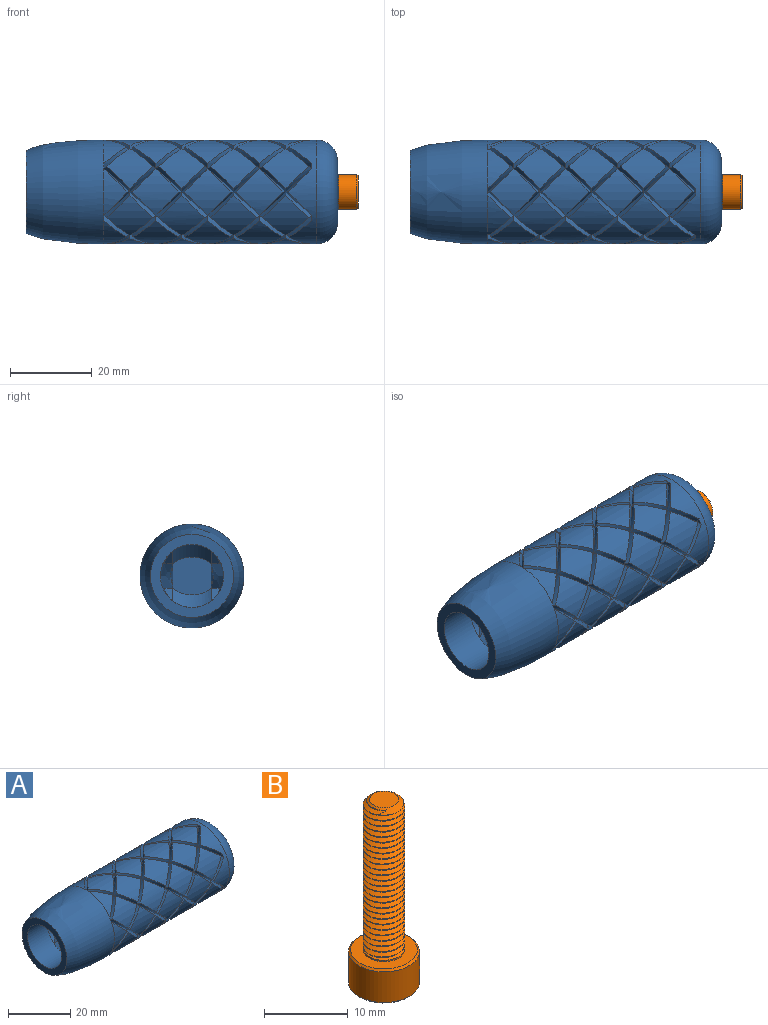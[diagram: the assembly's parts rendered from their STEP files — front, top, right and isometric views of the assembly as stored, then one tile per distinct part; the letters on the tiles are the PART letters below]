
ASSEMBLY  parts=2 mates=1
PART A: 280 faces, bbox 76.2x27.9x28 mm
  f0: bspline ~12.16x11.01mm, area 11.6mm2, adj f8,f18,f26,f229,f276
  f1: bspline ~17.6x16.24mm, area 11.6mm2, adj f9,f20,f22,f227
  f2: bspline ~12.16x11.01mm, area 11.6mm2, adj f10,f16,f24,f228
  f3: bspline ~12.16x9.32mm, area 11.6mm2, adj f11,f23,f225,f247
  f4: bspline ~12.16x9.32mm, area 11.6mm2, adj f12,f25,f30,f226
  f5: bspline ~12.16x10.1mm, area 11.6mm2, adj f13,f21,f29,f238
  f6: bspline ~12.16x11.3mm, area 11.6mm2, adj f14,f27,f31,f239
  f7: bspline ~12.16x11.7mm, area 11.6mm2, adj f15,f17,f28,f237
  f8: bspline ~12.16x11.01mm, area 11.6mm2, adj f0,f149,f242,f276
  f9: bspline ~12.16x11.79mm, area 11.6mm2, adj f1,f142,f145,f220
  f10: bspline ~12.16x11.01mm, area 11.6mm2, adj f2,f144,f147,f219
  f11: bspline ~12.16x9.32mm, area 11.6mm2, adj f3,f146,f154,f215
  f12: bspline ~12.16x9.32mm, area 11.6mm2, adj f4,f148,f166,f208
  f13: bspline ~17.6x12.62mm, area 11.6mm2, adj f5,f143,f165,f209
  f14: bspline ~12.16x11.3mm, area 11.6mm2, adj f6,f162,f167,f207
  f15: bspline ~12.16x11.7mm, area 11.6mm2, adj f7,f163,f164,f210
  f16: bspline ~12.16x11.01mm, area 11.6mm2, adj f2,f22,f118,f228
  f17: bspline ~17.6x16.57mm, area 11.6mm2, adj f7,f29,f55,f237
  f18: bspline ~12.16x11.01mm, area 11.6mm2, adj f0,f19,f117,f229,f276
  f19: bspline ~12.16x11.01mm, area 11.6mm2, adj f18,f119,f242,f276
  f20: bspline ~17.6x12.62mm, area 11.6mm2, adj f1,f21,f120,f227
  f21: bspline ~12.16x10.1mm, area 11.6mm2, adj f5,f20,f54,f238
  f22: bspline ~12.16x11.01mm, area 11.6mm2, adj f1,f16,f120,f227
  f23: bspline ~12.16x11.53mm, area 11.6mm2, adj f3,f24,f225,f245
  f24: bspline ~12.16x11.53mm, area 11.6mm2, adj f2,f23,f118,f228
  f25: bspline ~12.16x11.53mm, area 11.6mm2, adj f4,f26,f121,f226
  f26: bspline ~12.16x11.53mm, area 11.6mm2, adj f0,f25,f117,f229
  f27: bspline ~12.16x11.7mm, area 11.6mm2, adj f6,f28,f53,f239
  f28: bspline ~12.16x11.7mm, area 11.6mm2, adj f7,f27,f55,f237
  f29: bspline ~12.16x10.66mm, area 11.6mm2, adj f5,f17,f54,f238
  f30: bspline ~12.16x9.32mm, area 11.6mm2, adj f4,f31,f121,f226
  f31: bspline ~12.16x9.32mm, area 11.6mm2, adj f6,f30,f53,f239
  f32: bspline ~12.16x9.32mm, area 11.6mm2, adj f34,f107,f177,f201
  f33: bspline ~12.16x11.01mm, area 11.6mm2, adj f35,f175,f176,f202,f272
  f34: bspline ~12.16x9.32mm, area 11.6mm2, adj f32,f83,f191,f192
  f35: bspline ~12.16x11.01mm, area 11.6mm2, adj f33,f190,f242,f272
  f36: bspline ~17.6x16.24mm, area 11.6mm2, adj f39,f168,f173,f203
  f37: bspline ~12.16x9.32mm, area 11.6mm2, adj f40,f171,f205,f243
  f38: bspline ~12.16x11.01mm, area 11.6mm2, adj f41,f169,f170,f206
  f39: bspline ~12.16x11.79mm, area 11.6mm2, adj f36,f184,f188,f194
  f40: bspline ~12.16x9.32mm, area 11.6mm2, adj f37,f80,f187,f195
  f41: bspline ~12.16x11.01mm, area 11.6mm2, adj f38,f185,f186,f196
  f42: bspline ~12.16x11.7mm, area 11.6mm2, adj f43,f105,f242,f271
  f43: bspline ~12.16x11.7mm, area 11.6mm2, adj f42,f83,f191,f192,f271
  f44: bspline ~17.6x16.24mm, area 11.6mm2, adj f47,f178,f183,f197
  f45: bspline ~12.16x11.7mm, area 11.6mm2, adj f48,f97,f181,f199
  f46: bspline ~12.16x10.1mm, area 11.6mm2, adj f49,f179,f180,f200
  f47: bspline ~12.16x11.79mm, area 11.6mm2, adj f44,f184,f188,f194
  f48: bspline ~12.16x11.7mm, area 11.6mm2, adj f45,f80,f187,f195
  f49: bspline ~17.6x12.62mm, area 11.6mm2, adj f46,f185,f186,f196
  f50: bspline ~12.16x9.74mm, area 11.6mm2, adj f53,f178,f183,f197
  f51: bspline ~17.6x16.57mm, area 11.6mm2, adj f54,f97,f181,f199
  f52: bspline ~12.16x10.66mm, area 11.6mm2, adj f55,f179,f180,f200
  f53: bspline ~12.16x9.74mm, area 11.6mm2, adj f27,f31,f50,f239
  f54: bspline ~12.16x10.66mm, area 11.6mm2, adj f21,f29,f51,f238
  f55: bspline ~17.6x16.57mm, area 11.6mm2, adj f17,f28,f52,f237
  f56: bspline ~12.16x9.74mm, area 11.6mm2, adj f59,f156,f161,f211,f273
  f57: bspline ~12.16x11.53mm, area 11.6mm2, adj f60,f137,f159,f212
  f58: bspline ~12.16x11.53mm, area 11.6mm2, adj f61,f157,f158,f213
  f59: bspline ~12.16x9.74mm, area 11.6mm2, adj f56,f174,f242,f273
  f60: bspline ~12.16x11.53mm, area 11.6mm2, adj f57,f107,f177,f201
  f61: bspline ~12.16x11.53mm, area 11.6mm2, adj f58,f175,f176,f202
  f62: bspline ~12.16x9.74mm, area 11.6mm2, adj f64,f150,f153,f216
  f63: bspline ~12.16x11.53mm, area 11.6mm2, adj f65,f151,f218,f248
  f64: bspline ~12.16x9.74mm, area 11.6mm2, adj f62,f168,f173,f203
  f65: bspline ~12.16x11.53mm, area 11.6mm2, adj f63,f169,f170,f206
  f66: bspline ~12.16x11.3mm, area 11.6mm2, adj f69,f162,f167,f207
  f67: bspline ~12.16x11.01mm, area 11.6mm2, adj f70,f143,f165,f209
  f68: bspline ~12.16x9.32mm, area 11.6mm2, adj f71,f163,f164,f210
  f69: bspline ~12.16x11.3mm, area 11.6mm2, adj f66,f156,f161,f211
  f70: bspline ~12.16x11.01mm, area 11.6mm2, adj f67,f137,f159,f212
  f71: bspline ~12.16x9.32mm, area 11.6mm2, adj f68,f157,f158,f213
  f72: bspline ~12.16x11.3mm, area 11.6mm2, adj f73,f155,f214,f246
  f73: bspline ~12.16x11.3mm, area 11.6mm2, adj f72,f150,f153,f216
  f74: bspline ~12.16x11.7mm, area 11.6mm2, adj f76,f108,f111,f224
  f75: bspline ~12.16x11.3mm, area 11.6mm2, adj f77,f106,f109,f223
  f76: bspline ~12.16x11.7mm, area 11.6mm2, adj f74,f84,f87,f236
  f77: bspline ~12.16x11.3mm, area 11.6mm2, adj f75,f82,f85,f235
  f78: bspline ~12.16x10.1mm, area 11.6mm2, adj f79,f110,f172,f204
  f79: bspline ~17.6x12.62mm, area 11.6mm2, adj f78,f86,f189,f193
  f80: bspline ~12.16x11.3mm, area 11.6mm2, adj f40,f48,f81,f195
  f81: bspline ~12.16x11.3mm, area 11.6mm2, adj f80,f95,f234,f243
  f82: bspline ~12.16x11.3mm, area 11.6mm2, adj f77,f83,f93,f235
  f83: bspline ~12.16x11.3mm, area 11.6mm2, adj f34,f43,f82,f192
  f84: bspline ~12.16x11.3mm, area 11.6mm2, adj f76,f85,f92,f236
  f85: bspline ~12.16x11.3mm, area 11.6mm2, adj f77,f84,f93,f235
  f86: bspline ~12.16x9.74mm, area 11.6mm2, adj f79,f87,f89,f193
  f87: bspline ~12.16x9.74mm, area 11.6mm2, adj f76,f86,f92,f236
  f88: bspline ~12.16x11.01mm, area 11.6mm2, adj f89,f102,f182,f198
  f89: bspline ~12.16x11.01mm, area 11.6mm2, adj f86,f88,f189,f193
  f90: bspline ~12.16x9.32mm, area 11.6mm2, adj f92,f100,f103,f233
  f91: bspline ~12.16x11.3mm, area 11.6mm2, adj f93,f101,f104,f231
  f92: bspline ~12.16x9.32mm, area 11.6mm2, adj f84,f87,f90,f236
  f93: bspline ~12.16x11.3mm, area 11.6mm2, adj f82,f85,f91,f235
  f94: bspline ~12.16x11.3mm, area 11.6mm2, adj f95,f96,f99,f230
  f95: bspline ~12.16x11.3mm, area 11.6mm2, adj f81,f94,f234,f244
  f96: bspline ~12.16x11.7mm, area 11.6mm2, adj f94,f97,f115,f230
  f97: bspline ~12.16x11.7mm, area 11.6mm2, adj f45,f51,f96,f199
  f98: bspline ~12.16x9.32mm, area 11.6mm2, adj f99,f113,f232,f244
  f99: bspline ~12.16x9.32mm, area 11.6mm2, adj f94,f98,f115,f230
  f100: bspline ~12.16x9.32mm, area 11.6mm2, adj f90,f101,f112,f233
  f101: bspline ~12.16x9.32mm, area 11.6mm2, adj f91,f100,f114,f231
  f102: bspline ~12.16x11.53mm, area 11.6mm2, adj f88,f103,f116,f198
  f103: bspline ~12.16x11.53mm, area 11.6mm2, adj f90,f102,f112,f233
  f104: bspline ~12.16x11.7mm, area 11.6mm2, adj f91,f105,f114,f231,f275
  f105: bspline ~12.16x11.7mm, area 11.6mm2, adj f42,f104,f242,f275
  f106: bspline ~12.16x9.32mm, area 11.6mm2, adj f75,f107,f125,f223
  f107: bspline ~12.16x9.32mm, area 11.6mm2, adj f32,f60,f106,f201
  f108: bspline ~12.16x11.7mm, area 11.6mm2, adj f74,f109,f124,f224
  f109: bspline ~12.16x11.7mm, area 11.6mm2, adj f75,f108,f125,f223
  f110: bspline ~12.16x10.66mm, area 11.6mm2, adj f78,f111,f127,f204
  f111: bspline ~17.6x16.57mm, area 11.6mm2, adj f74,f110,f124,f224
  f112: bspline ~12.16x11.53mm, area 11.6mm2, adj f100,f103,f117,f233
  f113: bspline ~12.16x11.53mm, area 11.6mm2, adj f98,f118,f232,f245
  f114: bspline ~12.16x9.74mm, area 11.6mm2, adj f101,f104,f119,f231,f275
  f115: bspline ~12.16x9.74mm, area 11.6mm2, adj f96,f99,f120,f230
  f116: bspline ~12.16x11.53mm, area 11.6mm2, adj f102,f121,f182,f198
  f117: bspline ~12.16x11.53mm, area 11.6mm2, adj f18,f26,f112,f229
  f118: bspline ~12.16x11.53mm, area 11.6mm2, adj f16,f24,f113,f228
  f119: bspline ~12.16x9.74mm, area 11.6mm2, adj f19,f114,f242,f275
  f120: bspline ~12.16x9.74mm, area 11.6mm2, adj f20,f22,f115,f227
  f121: bspline ~12.16x11.53mm, area 11.6mm2, adj f25,f30,f116,f226
  f122: bspline ~12.16x10.66mm, area 11.6mm2, adj f124,f138,f141,f221
  f123: bspline ~12.16x9.74mm, area 11.6mm2, adj f125,f136,f139,f222
  f124: bspline ~17.6x16.57mm, area 11.6mm2, adj f108,f111,f122,f224
  f125: bspline ~12.16x9.74mm, area 11.6mm2, adj f106,f109,f123,f223
  f126: bspline ~17.6x16.57mm, area 11.6mm2, adj f127,f140,f152,f217
  f127: bspline ~12.16x10.66mm, area 11.6mm2, adj f110,f126,f172,f204
  f128: bspline ~17.6x12.62mm, area 11.6mm2, adj f131,f144,f147,f219
  f129: bspline ~12.16x11.79mm, area 11.6mm2, adj f132,f142,f145,f220
  f130: bspline ~12.16x11.7mm, area 11.6mm2, adj f133,f148,f166,f208,f274
  f131: bspline ~12.16x10.1mm, area 11.6mm2, adj f128,f138,f141,f221
  f132: bspline ~17.6x16.24mm, area 11.6mm2, adj f129,f136,f139,f222
  f133: bspline ~12.16x11.7mm, area 11.6mm2, adj f130,f160,f242,f274
  f134: bspline ~12.16x11.7mm, area 11.6mm2, adj f135,f146,f154,f215
  f135: bspline ~12.16x11.7mm, area 11.6mm2, adj f134,f140,f152,f217
  f136: bspline ~12.16x11.01mm, area 11.6mm2, adj f123,f132,f137,f222
  f137: bspline ~12.16x11.01mm, area 11.6mm2, adj f57,f70,f136,f212
  f138: bspline ~12.16x10.1mm, area 11.6mm2, adj f122,f131,f139,f221
  f139: bspline ~17.6x12.62mm, area 11.6mm2, adj f123,f132,f138,f222
  f140: bspline ~17.6x16.57mm, area 11.6mm2, adj f126,f135,f141,f217
  f141: bspline ~12.16x10.66mm, area 11.6mm2, adj f122,f131,f140,f221
  f142: bspline ~12.16x11.79mm, area 11.6mm2, adj f9,f129,f143,f220
  f143: bspline ~17.6x16.24mm, area 11.6mm2, adj f13,f67,f142,f209
  f144: bspline ~17.6x16.24mm, area 11.6mm2, adj f10,f128,f145,f219
  f145: bspline ~12.16x11.79mm, area 11.6mm2, adj f9,f129,f144,f220
  f146: bspline ~12.16x9.74mm, area 11.6mm2, adj f11,f134,f147,f215
  f147: bspline ~12.16x9.74mm, area 11.6mm2, adj f10,f128,f146,f219
  f148: bspline ~12.16x9.74mm, area 11.6mm2, adj f12,f130,f149,f208,f274
  f149: bspline ~12.16x9.74mm, area 11.6mm2, adj f8,f148,f242,f274
  f150: bspline ~12.16x9.32mm, area 11.6mm2, adj f62,f73,f151,f216
  f151: bspline ~12.16x9.32mm, area 11.6mm2, adj f63,f150,f218,f246
  f152: bspline ~12.16x11.7mm, area 11.6mm2, adj f126,f135,f153,f217
  f153: bspline ~12.16x11.7mm, area 11.6mm2, adj f62,f73,f152,f216
  f154: bspline ~12.16x11.3mm, area 11.6mm2, adj f11,f134,f155,f215
  f155: bspline ~12.16x11.3mm, area 11.6mm2, adj f72,f154,f214,f247
  f156: bspline ~12.16x9.32mm, area 11.6mm2, adj f56,f69,f157,f211
  f157: bspline ~12.16x9.32mm, area 11.6mm2, adj f58,f71,f156,f213
  f158: bspline ~12.16x11.53mm, area 11.6mm2, adj f58,f71,f159,f213
  f159: bspline ~12.16x11.53mm, area 11.6mm2, adj f57,f70,f158,f212
  f160: bspline ~12.16x11.7mm, area 11.6mm2, adj f133,f161,f242,f273
  f161: bspline ~12.16x11.7mm, area 11.6mm2, adj f56,f69,f160,f211,f273
  f162: bspline ~12.16x11.3mm, area 11.6mm2, adj f14,f66,f163,f207
  f163: bspline ~12.16x11.3mm, area 11.6mm2, adj f15,f68,f162,f210
  f164: bspline ~12.16x9.74mm, area 11.6mm2, adj f15,f68,f165,f210
  f165: bspline ~12.16x9.74mm, area 11.6mm2, adj f13,f67,f164,f209
  f166: bspline ~12.16x11.3mm, area 11.6mm2, adj f12,f130,f167,f208
  f167: bspline ~12.16x11.3mm, area 11.6mm2, adj f14,f66,f166,f207
  f168: bspline ~12.16x11.01mm, area 11.6mm2, adj f36,f64,f169,f203
  f169: bspline ~12.16x11.01mm, area 11.6mm2, adj f38,f65,f168,f206
  f170: bspline ~12.16x11.53mm, area 11.6mm2, adj f38,f65,f171,f206
  f171: bspline ~12.16x11.53mm, area 11.6mm2, adj f37,f170,f205,f248
  f172: bspline ~12.16x10.1mm, area 11.6mm2, adj f78,f127,f173,f204
  f173: bspline ~17.6x12.62mm, area 11.6mm2, adj f36,f64,f172,f203
  f174: bspline ~12.16x11.01mm, area 11.6mm2, adj f59,f175,f242,f272
  f175: bspline ~12.16x11.01mm, area 11.6mm2, adj f33,f61,f174,f202,f272
  f176: bspline ~12.16x11.53mm, area 11.6mm2, adj f33,f61,f177,f202
  f177: bspline ~12.16x11.53mm, area 11.6mm2, adj f32,f60,f176,f201
  f178: bspline ~17.6x12.62mm, area 11.6mm2, adj f44,f50,f179,f197
  f179: bspline ~12.16x10.1mm, area 11.6mm2, adj f46,f52,f178,f200
  f180: bspline ~12.16x10.66mm, area 11.6mm2, adj f46,f52,f181,f200
  f181: bspline ~17.6x16.57mm, area 11.6mm2, adj f45,f51,f180,f199
  f182: bspline ~12.16x11.01mm, area 11.6mm2, adj f88,f116,f183,f198
  f183: bspline ~12.16x11.01mm, area 11.6mm2, adj f44,f50,f182,f197
  f184: bspline ~12.16x11.79mm, area 11.6mm2, adj f39,f47,f185,f194
  f185: bspline ~17.6x16.24mm, area 11.6mm2, adj f41,f49,f184,f196
  f186: bspline ~12.16x9.74mm, area 11.6mm2, adj f41,f49,f187,f196
  f187: bspline ~12.16x9.74mm, area 11.6mm2, adj f40,f48,f186,f195
  f188: bspline ~12.16x11.79mm, area 11.6mm2, adj f39,f47,f189,f194
  f189: bspline ~17.6x16.24mm, area 11.6mm2, adj f79,f89,f188,f193
  f190: bspline ~12.16x9.74mm, area 11.6mm2, adj f35,f191,f242,f271
  f191: bspline ~12.16x9.74mm, area 11.6mm2, adj f34,f43,f190,f192,f271
  f192: cylinder r=12.7mm len=11.24mm, axis (-1,0,0), area 66.2mm2, adj f34,f43,f83,f191
  f193: cylinder r=12.7mm len=11.23mm, axis (-1,0,0), area 66mm2, adj f79,f86,f89,f189
  f194: cylinder r=12.7mm len=11.33mm, axis (-1,0,0), area 65.9mm2, adj f39,f47,f184,f188
  f195: cylinder r=12.7mm len=11.24mm, axis (-1,0,0), area 66.2mm2, adj f40,f48,f80,f187
  f196: cylinder r=12.7mm len=11.23mm, axis (-1,0,0), area 66mm2, adj f41,f49,f185,f186
  f197: cylinder r=12.7mm len=11.23mm, axis (-1,0,0), area 66mm2, adj f44,f50,f178,f183
  f198: cylinder r=12.7mm len=11.35mm, axis (-1,0,0), area 66.2mm2, adj f88,f102,f116,f182
  f199: cylinder r=12.7mm len=11.34mm, axis (-1,0,0), area 66mm2, adj f45,f51,f97,f181
  f200: cylinder r=12.7mm len=11.22mm, axis (-1,0,0), area 65.9mm2, adj f46,f52,f179,f180
  f201: cylinder r=12.7mm len=11.25mm, axis (-1,0,0), area 66.2mm2, adj f32,f60,f107,f177
  f202: cylinder r=12.7mm len=11.35mm, axis (-1,0,0), area 66.2mm2, adj f33,f61,f175,f176
  f203: cylinder r=12.7mm len=11.23mm, axis (-1,0,0), area 66mm2, adj f36,f64,f168,f173
  f204: cylinder r=12.7mm len=11.22mm, axis (-1,0,0), area 65.9mm2, adj f78,f110,f127,f172
  f205: cylinder r=12.7mm len=9.84mm, axis (-1,0,0), area 33.1mm2, adj f37,f171,f270
  f206: cylinder r=12.7mm len=11.35mm, axis (-1,0,0), area 66.2mm2, adj f38,f65,f169,f170
  f207: cylinder r=12.7mm len=11.36mm, axis (-1,0,0), area 66.2mm2, adj f14,f66,f162,f167
  f208: cylinder r=12.7mm len=11.24mm, axis (-1,0,0), area 66.2mm2, adj f12,f130,f148,f166
  f209: cylinder r=12.7mm len=11.23mm, axis (-1,0,0), area 66mm2, adj f13,f67,f143,f165
  f210: cylinder r=12.7mm len=11.24mm, axis (-1,0,0), area 66.2mm2, adj f15,f68,f163,f164
  f211: cylinder r=12.7mm len=11.24mm, axis (-1,0,0), area 66.2mm2, adj f56,f69,f156,f161
  f212: cylinder r=12.7mm len=11.35mm, axis (-1,0,0), area 66.2mm2, adj f57,f70,f137,f159
  f213: cylinder r=12.7mm len=11.25mm, axis (-1,0,0), area 66.2mm2, adj f58,f71,f157,f158
  f214: cylinder r=12.7mm len=11.36mm, axis (-1,0,0), area 33.1mm2, adj f72,f155,f270
  f215: cylinder r=12.7mm len=11.24mm, axis (-1,0,0), area 66.2mm2, adj f11,f134,f146,f154
  f216: cylinder r=12.7mm len=11.24mm, axis (-1,0,0), area 66.2mm2, adj f62,f73,f150,f153
  f217: cylinder r=12.7mm len=11.34mm, axis (-1,0,0), area 66mm2, adj f126,f135,f140,f152
  f218: cylinder r=12.7mm len=9.84mm, axis (-1,0,0), area 33.1mm2, adj f63,f151,f270
  f219: cylinder r=12.7mm len=11.23mm, axis (-1,0,0), area 66mm2, adj f10,f128,f144,f147
  f220: cylinder r=12.7mm len=11.33mm, axis (-1,0,0), area 65.9mm2, adj f9,f129,f142,f145
  f221: cylinder r=12.7mm len=11.22mm, axis (-1,0,0), area 65.9mm2, adj f122,f131,f138,f141
  f222: cylinder r=12.7mm len=11.23mm, axis (-1,0,0), area 66mm2, adj f123,f132,f136,f139
  f223: cylinder r=12.7mm len=11.24mm, axis (-1,0,0), area 66.2mm2, adj f75,f106,f109,f125
  f224: cylinder r=12.7mm len=11.34mm, axis (-1,0,0), area 66mm2, adj f74,f108,f111,f124
  f225: cylinder r=12.7mm len=9.84mm, axis (-1,0,0), area 33.1mm2, adj f3,f23,f270
  f226: cylinder r=12.7mm len=11.25mm, axis (-1,0,0), area 66.2mm2, adj f4,f25,f30,f121
  f227: cylinder r=12.7mm len=11.23mm, axis (-1,0,0), area 66mm2, adj f1,f20,f22,f120
  f228: cylinder r=12.7mm len=11.35mm, axis (-1,0,0), area 66.2mm2, adj f2,f16,f24,f118
  f229: cylinder r=12.7mm len=11.35mm, axis (-1,0,0), area 66.2mm2, adj f0,f18,f26,f117
  f230: cylinder r=12.7mm len=11.24mm, axis (-1,0,0), area 66.2mm2, adj f94,f96,f99,f115
  f231: cylinder r=12.7mm len=11.24mm, axis (-1,0,0), area 66.2mm2, adj f91,f101,f104,f114
  f232: cylinder r=12.7mm len=9.84mm, axis (-1,0,0), area 33.1mm2, adj f98,f113,f270
  f233: cylinder r=12.7mm len=11.25mm, axis (-1,0,0), area 66.2mm2, adj f90,f100,f103,f112
  f234: cylinder r=12.7mm len=11.36mm, axis (-1,0,0), area 33.1mm2, adj f81,f95,f270
  f235: cylinder r=12.7mm len=11.36mm, axis (-1,0,0), area 66.2mm2, adj f77,f82,f85,f93
  f236: cylinder r=12.7mm len=11.24mm, axis (-1,0,0), area 66.2mm2, adj f76,f84,f87,f92
  f237: cylinder r=12.7mm len=11.34mm, axis (-1,0,0), area 66mm2, adj f7,f17,f28,f55
  f238: cylinder r=12.7mm len=11.22mm, axis (-1,0,0), area 65.9mm2, adj f5,f21,f29,f54
  f239: cylinder r=12.7mm len=11.24mm, axis (-1,0,0), area 66.2mm2, adj f6,f27,f31,f53
  f240: plane 15.24x15.24mm, normal (1,0,0), area 160.4mm2, adj f241,f277
  f241: torus R=7.62mm, axis (-1,0,0), area 544.2mm2, adj f240,f242
  f242: cylinder r=12.7mm len=25.4mm, axis (-1,0,0), area 299mm2, adj f8,f19,f35,f42,f59,f105,f119,f133
  f243: plane 1.47x1.33mm, normal (1,0,0), area 0.9mm2, adj f37,f81,f270
  f244: plane 1.47x1.33mm, normal (1,0,0), area 0.9mm2, adj f95,f98,f270
  f245: plane 1.53x1.28mm, normal (1,0,0), area 0.9mm2, adj f23,f113,f270
  f246: plane 1.47x1.33mm, normal (1,0,0), area 0.9mm2, adj f72,f151,f270
  f247: plane 1.47x1.33mm, normal (1,0,0), area 0.9mm2, adj f3,f155,f270
  f248: plane 1.53x1.28mm, normal (1,0,0), area 0.9mm2, adj f63,f171,f270
  f249: plane 9.53x9.27mm, normal (-1,0,0), area 78.4mm2, adj f250,f254,f255,f256,f262,f263
  f250: cylinder r=7.73mm len=38.11mm, axis (1,0,0), area 391.3mm2, adj f249,f253,f254,f258,f263,f264
  f251: plane 29.73x2.14mm, normal (0,0,-1), area 31.8mm2, adj f256,f257,f265
  f252: plane 3.09x3.09mm, normal (-0.71,0,0.71), area 5.6mm2, adj f253,f264,f265
  f253: plane 29.73x2.14mm, normal (0,0,1), area 31.8mm2, adj f250,f252,f265
  f254: plane 8.39x2.99mm, normal (0,1,0), area 8.2mm2, adj f249,f250,f265
  f255: plane 8.39x2.99mm, normal (0,1,0), area 8.2mm2, adj f249,f256,f265
  f256: cylinder r=7.73mm len=38.11mm, axis (1,0,0), area 391.3mm2, adj f249,f251,f255,f261,f262,f266
  f257: plane 3.09x3.09mm, normal (-0.71,0,-0.71), area 5.6mm2, adj f251,f265,f266
  f258: plane 29.73x2.14mm, normal (0,0,1), area 31.8mm2, adj f250,f259,f267
  f259: plane 3.09x3.09mm, normal (-0.71,0,0.71), area 5.6mm2, adj f258,f264,f267
  f260: plane 3.09x3.09mm, normal (-0.71,0,-0.71), area 5.6mm2, adj f261,f266,f267
  f261: plane 29.73x2.14mm, normal (0,0,-1), area 31.8mm2, adj f256,f260,f267
  f262: plane 8.39x2.99mm, normal (0,-1,0), area 8.2mm2, adj f249,f256,f267
  f263: plane 8.39x2.99mm, normal (0,-1,0), area 8.2mm2, adj f249,f250,f267
  f264: bspline ~9.53x5.37mm, area 43.3mm2, adj f250,f252,f259,f268
  f265: bspline ~41.2x12.16mm, area 247.8mm2, adj f251,f252,f253,f254,f255,f257,f268
  f266: bspline ~9.53x5.37mm, area 43.3mm2, adj f256,f257,f260,f268
  f267: bspline ~41.2x12.16mm, area 247.8mm2, adj f258,f259,f260,f261,f262,f263,f268
  f268: cylinder r=7.73mm len=15.45mm, axis (1,0,0), area 449.9mm2, adj f264,f265,f266,f267,f269
  f269: plane 20.32x20.32mm, normal (-1,0,0), area 136.8mm2, adj f268,f270
  f270: revolved ~25.4x25.4mm, area 1459.6mm2, adj f205,f214,f218,f225,f232,f234,f243,f244
  f271: plane 1.48x1.34mm, normal (-1,0,0), area 1mm2, adj f42,f43,f190,f191,f242
  f272: plane 1.55x1.28mm, normal (-1,0,0), area 1mm2, adj f33,f35,f174,f175,f242
  f273: plane 1.48x1.34mm, normal (-1,0,0), area 1mm2, adj f56,f59,f160,f161,f242
  f274: plane 1.48x1.34mm, normal (-1,0,0), area 1mm2, adj f130,f133,f148,f149,f242
  f275: plane 1.48x1.34mm, normal (-1,0,0), area 1mm2, adj f104,f105,f114,f119,f242
  f276: plane 1.55x1.28mm, normal (-1,0,0), area 1mm2, adj f0,f8,f18,f19,f242
  f277: cylinder r=2.65mm len=20.23mm, axis (1,0,0), area 336.8mm2, adj f240,f279
  f278: plane 1.3x1.3mm, normal (1,0,0), area 1.3mm2, adj f279
  f279: cone r=0.65mm half-angle=45deg, axis (1,0,0), area 29.3mm2, adj f277,f278
PART B: 51 faces, bbox 9.4x9.4x28 mm
  f0: cone r=2.5mm half-angle=67.5deg, axis (0,0,-1), area 4.1mm2, adj f1,f30,f31,f50
  f1: cylinder r=1.98mm len=21.41mm, axis (0,0,-1), area 33.3mm2, adj f0,f2,f30,f50
  f2: cone r=1.73mm half-angle=55deg, axis (0,0,-1), area 7.9mm2, adj f1,f3,f4,f30,f50
  f3: plane 3.45x3.45mm, normal (0,0,1), area 9.4mm2, adj f2
  f4: cylinder r=2.5mm len=5mm, axis (0,0,1), area 1mm2, adj f2,f5,f30,f50
  f5: cylinder r=2.5mm len=5mm, axis (0,0,1), area 1.6mm2, adj f4,f6,f30,f50
  f6: cylinder r=2.5mm len=5mm, axis (0,0,1), area 1.6mm2, adj f5,f7,f30,f50
  f7: cylinder r=2.5mm len=5mm, axis (0,0,1), area 1.6mm2, adj f6,f8,f30,f50
  f8: cylinder r=2.5mm len=5mm, axis (0,0,1), area 1.6mm2, adj f7,f9,f30,f50
  f9: cylinder r=2.5mm len=5mm, axis (0,0,1), area 1.6mm2, adj f8,f10,f30,f50
  f10: cylinder r=2.5mm len=5mm, axis (0,0,1), area 1.6mm2, adj f9,f11,f30,f50
  f11: cylinder r=2.5mm len=5mm, axis (0,0,1), area 1.6mm2, adj f10,f12,f30,f50
  f12: cylinder r=2.5mm len=5mm, axis (0,0,1), area 1.6mm2, adj f11,f13,f30,f50
  f13: cylinder r=2.5mm len=5mm, axis (0,0,1), area 1.6mm2, adj f12,f14,f30,f50
  f14: cylinder r=2.5mm len=5mm, axis (0,0,1), area 1.6mm2, adj f13,f15,f30,f50
  f15: cylinder r=2.5mm len=5mm, axis (0,0,1), area 1.6mm2, adj f14,f16,f30,f50
  f16: cylinder r=2.5mm len=5mm, axis (0,0,1), area 1.6mm2, adj f15,f17,f30,f50
  f17: cylinder r=2.5mm len=5mm, axis (0,0,1), area 1.6mm2, adj f16,f18,f30,f50
  f18: cylinder r=2.5mm len=5mm, axis (0,0,1), area 1.6mm2, adj f17,f19,f30,f50
  f19: cylinder r=2.5mm len=5mm, axis (0,0,1), area 1.6mm2, adj f18,f20,f30,f50
  f20: cylinder r=2.5mm len=5mm, axis (0,0,1), area 1.6mm2, adj f19,f21,f30,f50
  f21: cylinder r=2.5mm len=5mm, axis (0,0,1), area 1.6mm2, adj f20,f22,f30,f50
  f22: cylinder r=2.5mm len=5mm, axis (0,0,1), area 1.6mm2, adj f21,f23,f30,f50
  f23: cylinder r=2.5mm len=5mm, axis (0,0,1), area 1.6mm2, adj f22,f24,f30,f50
  f24: cylinder r=2.5mm len=5mm, axis (0,0,1), area 1.6mm2, adj f23,f25,f30,f50
  f25: cylinder r=2.5mm len=5mm, axis (0,0,1), area 1.6mm2, adj f24,f26,f30,f50
  f26: cylinder r=2.5mm len=5mm, axis (0,0,1), area 1.6mm2, adj f25,f27,f30,f50
  f27: cylinder r=2.5mm len=5mm, axis (0,0,1), area 1.6mm2, adj f26,f28,f30,f50
  f28: cylinder r=2.5mm len=5mm, axis (0,0,1), area 1.6mm2, adj f27,f29,f30,f50
  f29: cylinder r=2.5mm len=5mm, axis (0,0,1), area 1.6mm2, adj f28,f30,f31,f50
  f30: bspline ~21.71x4.99mm, area 225.4mm2, adj f0,f1,f2,f4,f5,f6,f7,f8
  f31: cylinder r=2.5mm len=5mm, axis (0,0,1), area 4.6mm2, adj f0,f29,f30,f32,f50
  f32: plane 7.99x7.99mm, normal (0,0,1), area 30.5mm2, adj f31,f33
  f33: cone r=4.25mm half-angle=45deg, axis (0,0,-1), area 9.3mm2, adj f32,f34
  f34: cylinder r=4.25mm len=8.5mm, axis (0,0,1), area 119.9mm2, adj f33,f35
  f35: cone r=4mm half-angle=45deg, axis (0,0,1), area 9.3mm2, adj f34,f36
  f36: plane 8.74x8.74mm, normal (0,0,-1), area 33.4mm2, adj f35,f37,f45,f46,f47,f48,f49
  f37: cone r=2.31mm half-angle=45deg, axis (0,0,-1), area 0mm2, adj f36,f38
  f38: plane 3.88x2.88mm, normal (-0.5,-0.87,0), area 6.5mm2, adj f37,f39,f43,f44
  f39: plane 4.62x4mm, normal (0,0,-1), area 13.9mm2, adj f38,f40,f41,f42,f43,f44
  f40: plane 3.22x2.53mm, normal (1,0,0), area 6.5mm2, adj f39,f41,f44,f48
  f41: plane 3.88x2.88mm, normal (0.5,0.87,0), area 6.5mm2, adj f39,f40,f42,f47
  f42: plane 3.88x2.88mm, normal (-0.5,0.87,0), area 6.5mm2, adj f39,f41,f43,f46
  f43: plane 3.88x3.18mm, normal (-1,0,0), area 6.5mm2, adj f38,f39,f42,f45
  f44: plane 3.88x2.88mm, normal (0.5,-0.87,0), area 6.5mm2, adj f38,f39,f40,f49
  f45: cone r=2.31mm half-angle=45deg, axis (0,0,-1), area 0mm2, adj f36,f43
  f46: cone r=2.31mm half-angle=45deg, axis (0,0,-1), area 0mm2, adj f36,f42
  f47: cone r=2.31mm half-angle=45deg, axis (0,0,-1), area 0mm2, adj f36,f41
  f48: cone r=2.31mm half-angle=45deg, axis (0,0,-1), area 0.5mm2, adj f36,f40
  f49: cone r=2.31mm half-angle=45deg, axis (0,0,-1), area 0mm2, adj f36,f44
  f50: bspline ~22.22x5mm, area 225.4mm2, adj f0,f1,f2,f4,f5,f6,f7,f8
PLACE A t=(-34.3,2.81,0.92)mm
PLACE B rot(axis=(0.71,0,-0.71),180deg) t=(19.9,2.81,0.92)mm
MATE fastened B.f1 <-> A.f192  axis (-1,0,0) through (41.9,2.81,0.92)mm
